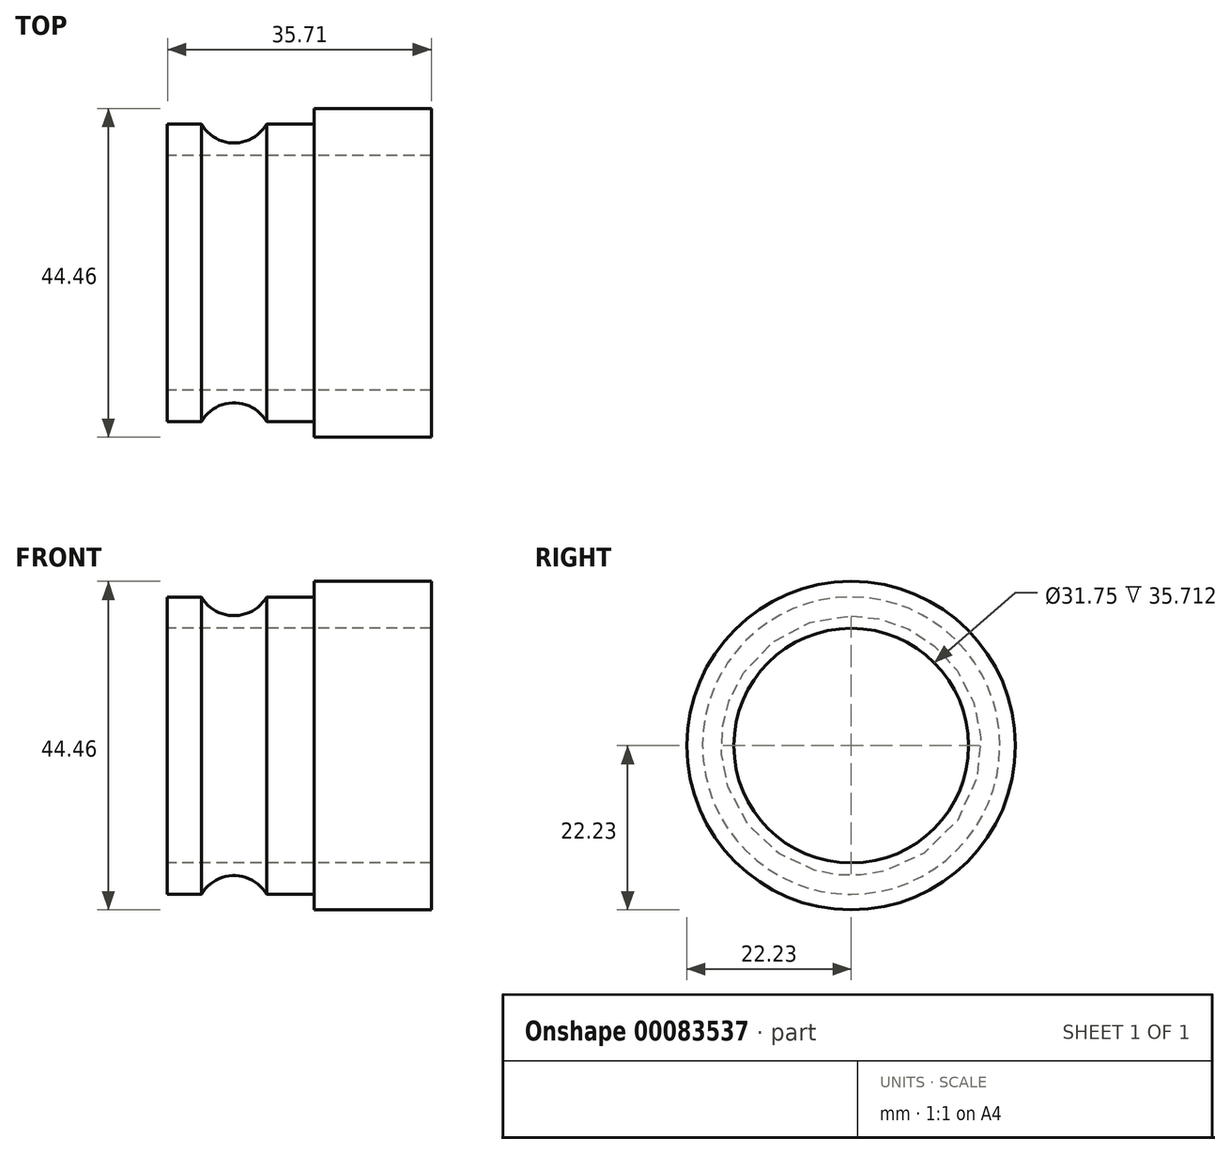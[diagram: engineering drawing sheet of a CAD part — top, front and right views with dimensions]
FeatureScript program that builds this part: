
annotation { "Feature Type Name" : "Feature", "Feature Type Description" : "" }
export const myFeature = defineFeature(function(context is Context, id is Id, definition is map)
    precondition{}
    {
        {
            var Q0;
            Q0=qCreatedBy(makeId("Front.planeOp"),FACE);
            var sketch = newSketch(context, id + "F0", { "sketchPlane" : qUnion([Q0])});
            skLineSegment(sketch, "E0", {"start": v(0, 0) * mm, "end": v(-9, 0) * mm});
            skLineSegment(sketch, "E1", {"start": v(0, 0) * mm, "end": v(10.83, 0) * mm});
            skLineSegment(sketch, "E2", {"start": v(10.83, 20.12) * mm, "end": v(4.4, 20.12) * mm});
            skLineSegment(sketch, "E3", {"start": v(-9, 20.12) * mm, "end": v(-9, 15.88) * mm});
            skArc(sketch, "E4", {"start": v(-4.4, 20.12) * mm, "mid": v(0, 17.58) * mm, "end": v(4.4, 20.12) * mm});
            skLineSegment(sketch, "E5.trimOffspring", {"start": v(-4.4, 20.12) * mm, "end": v(-9, 20.12) * mm});
            skPoint(sketch, "E6.orphan", {"position": v(0, 20.12) * mm});
            skLineSegment(sketch, "E7", {"start": v(10.83, 20.12) * mm, "end": v(10.83, 22.23) * mm});
            skPoint(sketch, "E7.endSnap0", {"position": v(10.83, 10.06) * mm});
            skLineSegment(sketch, "E8", {"start": v(10.83, 22.23) * mm, "end": v(26.7, 22.23) * mm});
            skLineSegment(sketch, "E9", {"start": v(26.7, 22.23) * mm, "end": v(26.7, 0) * mm});
            skLineSegment(sketch, "E10", {"start": v(26.7, 15.88) * mm, "end": v(-9, 15.88) * mm});
            skLineSegment(sketch, "E11", {"start": v(-9, 0) * mm, "end": v(-9, 20.12) * mm});
            skSolve(sketch);
        }
        {
            var Q0;
            Q0=makeQuery(id+"F0.imprint","IMPRINT",FACE,{"disambiguationData":[TD([[makeQuery(id+"F0.imprint","IMPRINT",EDGE,{"derivedFrom":sQuery(id+"F0.wireOp",EDGE,"E2")}),1.0]])]});
            var Q1;
            Q1=sQuery(id+"F0.wireOp",EDGE,"E1");
            revolve(context, id + "F1", {"entities" : qUnion([Q0]), "axis" : qUnion([Q1]), "revolveType" : RevolveType.FULL});
        }
    });
